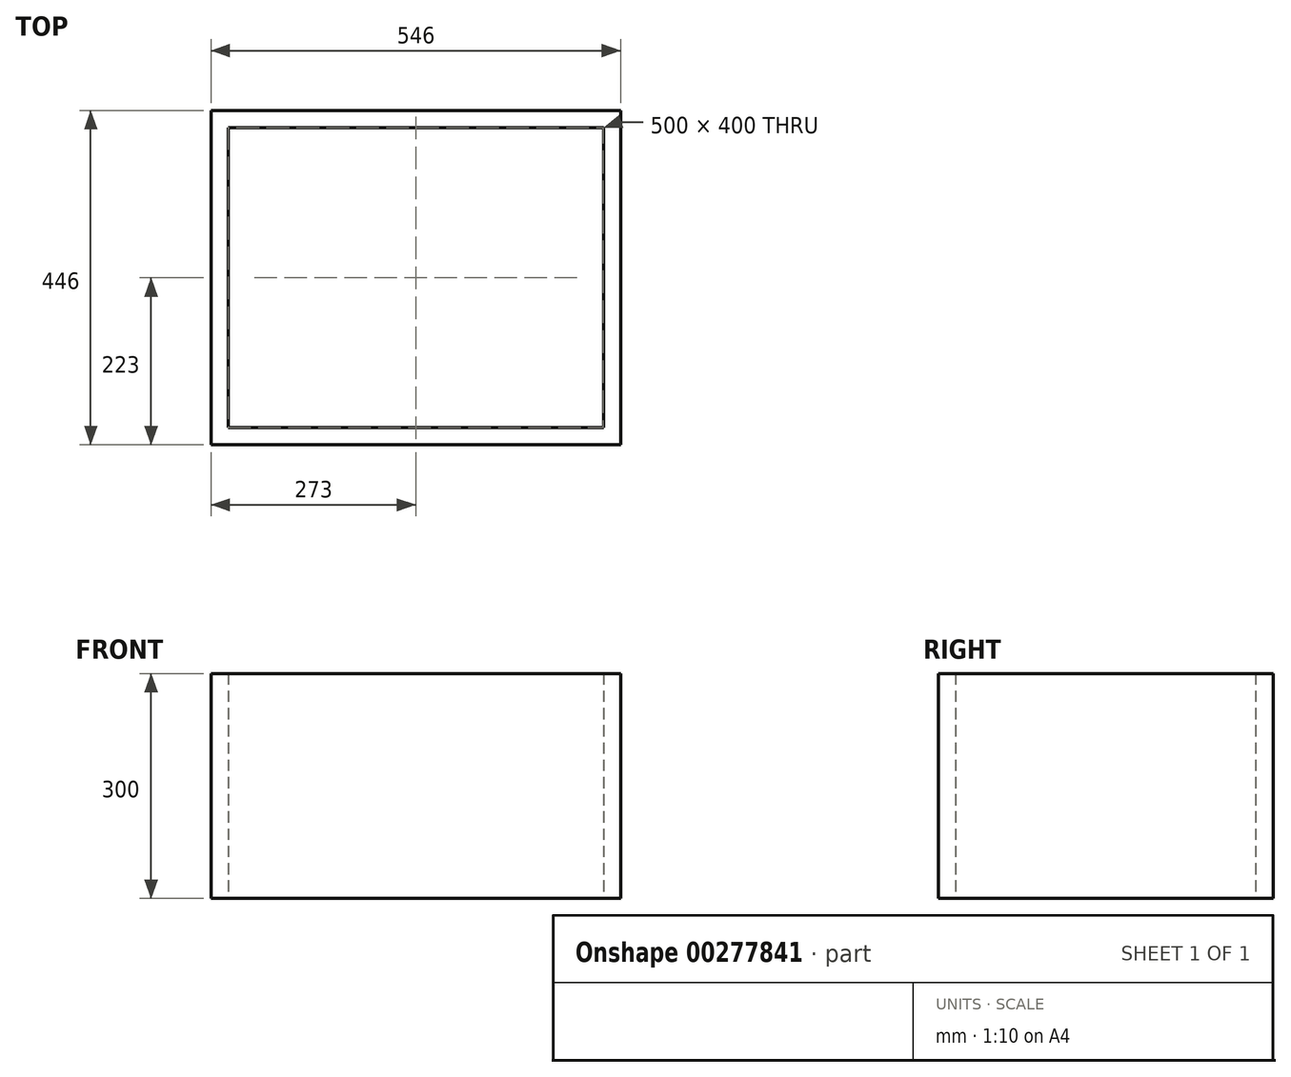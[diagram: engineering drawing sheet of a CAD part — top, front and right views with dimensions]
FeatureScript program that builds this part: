
annotation { "Feature Type Name" : "Feature", "Feature Type Description" : "" }
export const myFeature = defineFeature(function(context is Context, id is Id, definition is map)
    precondition{}
    {
        {
            var Q0;
            Q0=qCreatedBy(makeId("Top.planeOp"),FACE);
            var sketch = newSketch(context, id + "F0", { "sketchPlane" : qUnion([Q0])});
            skLineSegment(sketch, "E0.bottom", {"start": v(250, 200) * mm, "end": v(-250, 200) * mm});
            skLineSegment(sketch, "E0.top", {"start": v(250, -200) * mm, "end": v(-250, -200) * mm});
            skLineSegment(sketch, "E0.left", {"start": v(250, 200) * mm, "end": v(250, -200) * mm});
            skLineSegment(sketch, "E0.right", {"start": v(-250, 200) * mm, "end": v(-250, -200) * mm});
            skPoint(sketch, "E0.middle", {"position": v(0, 0) * mm});
            skSolve(sketch);
        }
        {
            var Q0;
            Q0=qCreatedBy(makeId("Top.planeOp"),FACE);
            var sketch = newSketch(context, id + "F1", { "sketchPlane" : qUnion([Q0])});
            skLineSegment(sketch, "E1.bottom", {"start": v(-250, 200) * mm, "end": v(-273, 200) * mm});
            skLineSegment(sketch, "E1.top", {"start": v(-250, -200) * mm, "end": v(-273, -200) * mm});
            skLineSegment(sketch, "E1.left", {"start": v(-250, 200) * mm, "end": v(-250, -200) * mm});
            skLineSegment(sketch, "E1.right", {"start": v(-273, 200) * mm, "end": v(-273, -200) * mm});
            skLineSegment(sketch, "E2.bottom", {"start": v(250, 200) * mm, "end": v(273, 200) * mm});
            skLineSegment(sketch, "E2.top", {"start": v(250, -200) * mm, "end": v(273, -200) * mm});
            skLineSegment(sketch, "E2.left", {"start": v(250, 200) * mm, "end": v(250, -200) * mm});
            skLineSegment(sketch, "E2.right", {"start": v(273, 200) * mm, "end": v(273, -200) * mm});
            skLineSegment(sketch, "E3.bottom", {"start": v(-273, 223) * mm, "end": v(273, 223) * mm});
            skLineSegment(sketch, "E3.top", {"start": v(-273, 200) * mm, "end": v(273, 200) * mm});
            skLineSegment(sketch, "E3.left", {"start": v(-273, 223) * mm, "end": v(-273, 200) * mm});
            skLineSegment(sketch, "E3.right", {"start": v(273, 223) * mm, "end": v(273, 200) * mm});
            skLineSegment(sketch, "E4.bottom", {"start": v(-273, -200) * mm, "end": v(273, -200) * mm});
            skLineSegment(sketch, "E4.top", {"start": v(-273, -223) * mm, "end": v(273, -223) * mm});
            skLineSegment(sketch, "E4.left", {"start": v(-273, -200) * mm, "end": v(-273, -223) * mm});
            skLineSegment(sketch, "E4.right", {"start": v(273, -200) * mm, "end": v(273, -223) * mm});
            skSolve(sketch);
        }
        {
            var Q0;
            Q0 = qSketchRegion(id + "F1", true);
            extrude(context, id + "F2", {"entities" : qUnion([Q0]), "depth" : 300 * mm});
        }
    });
